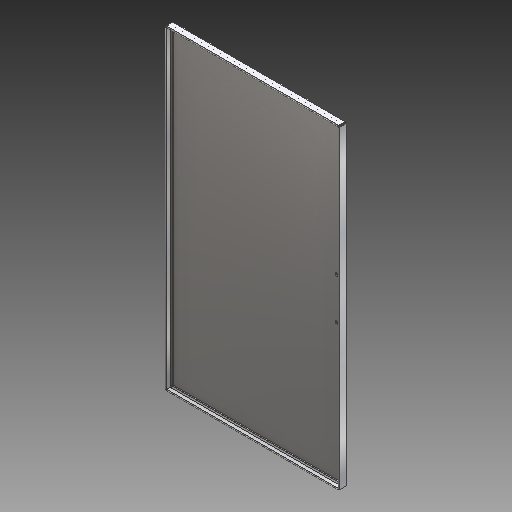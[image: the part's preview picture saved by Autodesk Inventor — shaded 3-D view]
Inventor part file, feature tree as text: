
AUTODESK INVENTOR PART (.ipt)
format: ipt  version: 2017 (Build 210142000, 142)  size: 304,128 bytes
history: native  units: in
note: dims shown in document units (in); Inventor stores cm internally (conversion verified against a paired STEP export)
features: sketch x10, other x5, plane x2, extrude x1, projected_geometry x1
ambient origin geometry x8: Origin, YZ Plane, XZ Plane, XY Plane, X Axis, Y Axis, Z Axis, Center Point
bodies: Solid1 (feature_tree)
feature tree (19):
  other  "Porta.ipt"
  extrude  "Extrusion2"  Depth=0.3937in
  plane  "Work Plane2"
  other  "Decal1"
  other  "Solid1::Porta.ipt"
  other  "TaggingFeature1"
  sketch  "Sketch1"  dims[d0=0.3937in d3=0.12in]
  sketch  "Sketch2"  dims[d4=0.0in]
  sketch  "Sketch4"  dims[d5=7.874in]
  sketch  "Sketch5"
  sketch  "Sketch6"
  sketch  "Sketch7"
  sketch  "Sketch8"
  sketch  "Sketch9"
  plane  "Work Plane1"
  sketch  "Sketch11"
  projected_geometry  "Projected Loop1"
  sketch  "Sketch12"
  other  "Image1"
